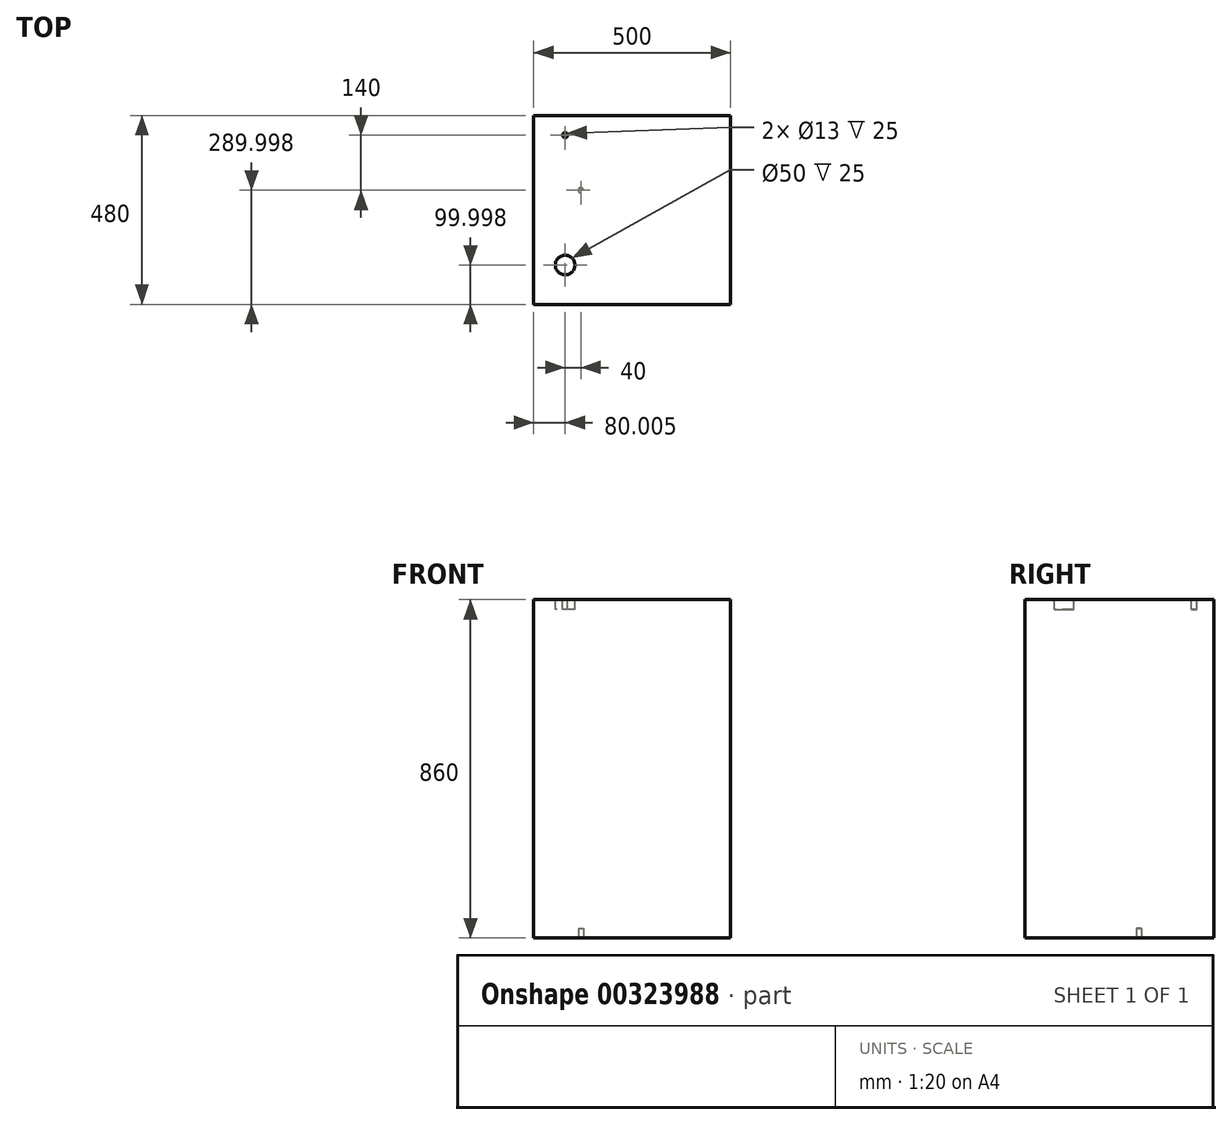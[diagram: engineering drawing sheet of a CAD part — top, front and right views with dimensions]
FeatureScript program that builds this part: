
annotation { "Feature Type Name" : "Feature", "Feature Type Description" : "" }
export const myFeature = defineFeature(function(context is Context, id is Id, definition is map)
    precondition{}
    {
        {
            var Q0;
            Q0=qCreatedBy(makeId("Top.planeOp"),FACE);
            var sketch = newSketch(context, id + "F0", { "sketchPlane" : qUnion([Q0])});
            skLineSegment(sketch, "E0.bottom", {"start": v(-264.18, 314.64) * mm, "end": v(235.82, 314.64) * mm});
            skLineSegment(sketch, "E0.top", {"start": v(-264.18, -165.36) * mm, "end": v(235.82, -165.36) * mm});
            skLineSegment(sketch, "E0.left", {"start": v(-264.18, 314.64) * mm, "end": v(-264.18, -165.36) * mm});
            skLineSegment(sketch, "E0.right", {"start": v(235.82, 314.64) * mm, "end": v(235.82, -165.36) * mm});
            skSolve(sketch);
        }
        {
            var Q0;
            Q0 = qSketchRegion(id + "F0", true);
            extrude(context, id + "F1", {"entities" : qUnion([Q0]), "oppositeDirection" : true, "depth" : 860 * mm});
        }
        {
            var Q0;
            Q0=makeQuery(id+"F1.opExtrude","CAP_FACE",FACE,{"disambiguationData":[OSD([sQuery(id+"F0.wireOp",EDGE,"E0.bottom"),sQuery(id+"F0.wireOp",EDGE,"E0.top"),sQuery(id+"F0.wireOp",EDGE,"E0.left"),sQuery(id+"F0.wireOp",EDGE,"E0.right")])],"isStart":true});
            var sketch = newSketch(context, id + "F2", { "sketchPlane" : qUnion([Q0])});
            skCircle(sketch, "E1", {"center": v(-184.18, -65.36) * mm, "radius": 25 * mm});
            skCircle(sketch, "E2", {"center": v(-184.18, 264.64) * mm, "radius": 6.5 * mm});
            skSolve(sketch);
        }
        {
            var Q0;
            Q0 = qSketchRegion(id + "F2", true);
            extrude(context, id + "F3", {"entities" : qUnion([Q0]), "operationType" : NewBodyOperationType.REMOVE, "oppositeDirection" : true, "depth" : 25 * mm});
        }
        {
            var Q0;
            Q0=makeQuery(id+"F1.opExtrude","CAP_FACE",FACE,{"disambiguationData":[OSD([sQuery(id+"F0.wireOp",EDGE,"E0.bottom"),sQuery(id+"F0.wireOp",EDGE,"E0.top"),sQuery(id+"F0.wireOp",EDGE,"E0.left"),sQuery(id+"F0.wireOp",EDGE,"E0.right")])],"isStart":false});
            var sketch = newSketch(context, id + "F4", { "sketchPlane" : qUnion([Q0])});
            skCircle(sketch, "E3", {"center": v(-144.18, -124.64) * mm, "radius": 6.5 * mm});
            skSolve(sketch);
        }
        {
            var Q0;
            Q0 = qSketchRegion(id + "F4", true);
            extrude(context, id + "F5", {"entities" : qUnion([Q0]), "operationType" : NewBodyOperationType.REMOVE, "oppositeDirection" : true, "depth" : 25 * mm});
        }
    });
